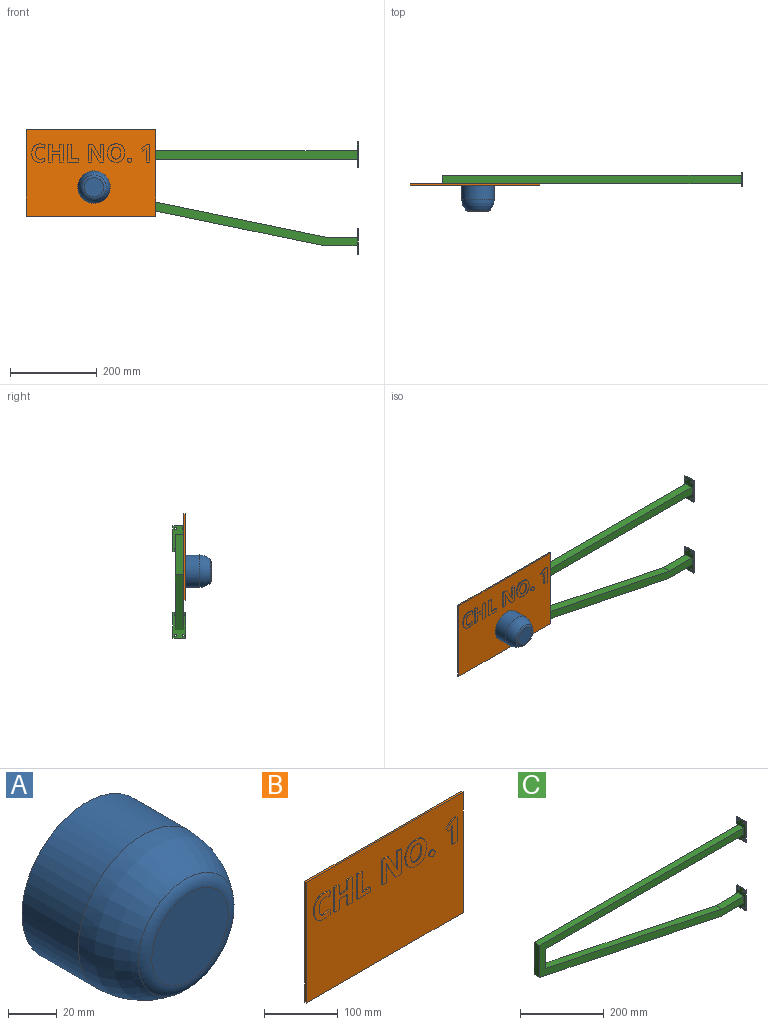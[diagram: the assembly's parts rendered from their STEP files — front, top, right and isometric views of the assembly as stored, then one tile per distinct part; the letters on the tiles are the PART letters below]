
ASSEMBLY  parts=3 mates=2
PART A: 5 faces, bbox 75x60x75 mm
  f0: cylinder r=37.5mm len=75mm, axis (0,1,0), area 7711.8mm2, adj f2,f4
  f1: plane 44.37x44.37mm, normal (0,-1,0), area 1546.4mm2, adj f3
  f2: plane 75x75mm, normal (0,1,0), area 4417.9mm2, adj f0
  f3: torus R=22.19mm, axis (0,-1,0), area 993.7mm2, adj f1,f4
  f4: torus R=0.5mm, axis (0,-1,0), area 5880.9mm2, adj f0,f3
PART B: 93 faces, bbox 300x5x200 mm
  f0: plane 300x200mm, normal (0,-1,0), area 55248.8mm2, adj f1,f2,f3,f4,f6,f7,f8,f9
  f1: plane 200x3mm, normal (1,0,0), area 600mm2, adj f0,f2,f4,f5
  f2: plane 300x3mm, normal (0,0,1), area 900mm2, adj f0,f1,f3,f5
  f3: plane 200x3mm, normal (-1,0,0), area 600mm2, adj f0,f2,f4,f5
  f4: plane 300x3mm, normal (0,0,-1), area 900mm2, adj f0,f1,f3,f5
  f5: plane 300x200mm, normal (0,1,0), area 60000mm2, adj f1,f2,f3,f4
  f6: extruded ~7.63x3.7mm, area 17.7mm2, adj f0,f7,f20,f21
  f7: extruded ~4.58x2mm, area 9.4mm2, adj f0,f6,f8,f21
  f8: extruded ~4.65x2mm, area 10.1mm2, adj f0,f7,f9,f21
  f9: plane 7.1x2.81mm, normal (0.93,0,-0.37), area 15.3mm2, adj f0,f8,f10,f21
  f10: extruded ~12.04x2.89mm, area 25mm2, adj f0,f9,f11,f21
  f11: extruded ~10.26x2.57mm, area 21.4mm2, adj f0,f10,f12,f21
  f12: extruded ~7.4x6.71mm, area 20.3mm2, adj f0,f11,f13,f21
  f13: extruded ~11.25x2.34mm, area 23.2mm2, adj f0,f12,f14,f21
  f14: extruded ~15.63x4.75mm, area 33.4mm2, adj f0,f13,f15,f21
  f15: extruded ~13.73x5.45mm, area 30.5mm2, adj f0,f14,f16,f21
  f16: extruded ~11.31x2.12mm, area 23.2mm2, adj f0,f15,f17,f21
  f17: plane 7.31x2mm, normal (1,0,0), area 14.6mm2, adj f0,f16,f18,f21
  f18: extruded ~10.49x2.16mm, area 21.5mm2, adj f0,f17,f19,f21
  f19: extruded ~13.76x10.33mm, area 39.3mm2, adj f0,f18,f20,f21
  f20: extruded ~10.31x2.7mm, area 21.7mm2, adj f0,f6,f19,f21
  f21: plane 42.29x31.34mm, normal (0,-1,0), area 594.2mm2, adj f6,f7,f8,f9,f10,f11,f12,f13
  f22: plane 8.7x2mm, normal (0,0,-1), area 17.4mm2, adj f0,f23,f33,f34
  f23: plane 41.14x2mm, normal (1,0,0), area 82.3mm2, adj f0,f22,f24,f34
  f24: plane 8.7x2mm, normal (0,0,1), area 17.4mm2, adj f0,f23,f25,f34
  f25: plane 16.13x2mm, normal (-1,0,0), area 32.3mm2, adj f0,f24,f26,f34
  f26: plane 16.29x2mm, normal (0,0,1), area 32.6mm2, adj f0,f25,f27,f34
  f27: plane 16.13x2mm, normal (1,0,0), area 32.3mm2, adj f0,f26,f28,f34
  f28: plane 8.72x2mm, normal (0,0,1), area 17.4mm2, adj f0,f27,f29,f34
  f29: plane 41.14x2mm, normal (-1,0,0), area 82.3mm2, adj f0,f28,f30,f34
  f30: plane 8.72x2mm, normal (0,0,-1), area 17.4mm2, adj f0,f29,f31,f34
  f31: plane 17.76x2mm, normal (1,0,0), area 35.5mm2, adj f0,f30,f32,f34
  f32: plane 16.29x2mm, normal (0,0,-1), area 32.6mm2, adj f0,f31,f33,f34
  f33: plane 17.76x2mm, normal (-1,0,0), area 35.5mm2, adj f0,f22,f32,f34
  f34: plane 41.14x33.71mm, normal (0,-1,0), area 834.9mm2, adj f22,f23,f24,f25,f26,f27,f28,f29
  f35: plane 41.14x2mm, normal (-1,0,0), area 82.3mm2, adj f0,f36,f40,f41
  f36: plane 25.41x2mm, normal (0,0,-1), area 50.8mm2, adj f0,f35,f37,f41
  f37: plane 7.2x2mm, normal (1,0,0), area 14.4mm2, adj f0,f36,f38,f41
  f38: plane 16.68x2mm, normal (0,0,1), area 33.4mm2, adj f0,f37,f39,f41
  f39: plane 33.94x2mm, normal (1,0,0), area 67.9mm2, adj f0,f38,f40,f41
  f40: plane 8.72x2mm, normal (0,0,1), area 17.4mm2, adj f0,f35,f39,f41
  f41: plane 41.14x25.41mm, normal (0,-1,0), area 479.1mm2, adj f35,f36,f37,f38,f39,f40
  f42: plane 11.08x2mm, normal (0,0,-1), area 22.2mm2, adj f0,f43,f55,f56
  f43: plane 41.14x2mm, normal (1,0,0), area 82.3mm2, adj f0,f42,f44,f56
  f44: plane 7.85x2mm, normal (0,0,1), area 15.7mm2, adj f0,f43,f45,f56
  f45: plane 19.48x2mm, normal (-1,0,0), area 39mm2, adj f0,f44,f46,f56
  f46: extruded ~11.34x2mm, area 22.7mm2, adj f0,f45,f47,f56
  f47: plane 2x0.2mm, normal (0,0,1), area 0.4mm2, adj f0,f46,f48,f56
  f48: plane 30.81x17.86mm, normal (0.87,0,0.5), area 71.2mm2, adj f0,f47,f49,f56
  f49: plane 11x2mm, normal (0,0,1), area 22mm2, adj f0,f48,f50,f56
  f50: plane 41.14x2mm, normal (-1,0,0), area 82.3mm2, adj f0,f49,f51,f56
  f51: plane 7.8x2mm, normal (0,0,-1), area 15.6mm2, adj f0,f50,f52,f56
  f52: plane 19.36x2mm, normal (1,0,0), area 38.7mm2, adj f0,f51,f53,f56
  f53: extruded ~11.76x2mm, area 23.5mm2, adj f0,f52,f54,f56
  f54: plane 2x0.25mm, normal (0,0,-1), area 0.5mm2, adj f0,f53,f55,f56
  f55: plane 31.12x17.9mm, normal (-0.87,0,-0.5), area 71.8mm2, adj f0,f42,f54,f56
  f56: plane 41.14x36.49mm, normal (0,-1,0), area 959mm2, adj f42,f43,f44,f45,f46,f47,f48,f49
  f57: extruded ~10.39x2.62mm, area 21.8mm2, adj f58,f70,f71,f72
  f58: extruded ~10.39x2.64mm, area 21.8mm2, adj f57,f59,f71,f72
  f59: extruded ~7.85x3.5mm, area 17.9mm2, adj f58,f60,f71,f72
  f60: extruded ~13.89x10.38mm, area 39.6mm2, adj f59,f61,f71,f72
  f61: extruded ~13.88x10.44mm, area 39.6mm2, adj f60,f70,f71,f72
  f62: extruded ~15.71x5.06mm, area 33.8mm2, adj f0,f63,f69,f71
  f63: extruded ~15.7x5.02mm, area 33.8mm2, adj f0,f62,f64,f71
  f64: extruded ~14.51x5.46mm, area 31.9mm2, adj f0,f63,f65,f71
  f65: extruded ~14.56x5.42mm, area 32mm2, adj f0,f64,f66,f71
  f66: extruded ~15.69x5.08mm, area 33.8mm2, adj f0,f65,f67,f71
  f67: extruded ~15.76x5.06mm, area 33.9mm2, adj f0,f66,f68,f71
  f68: extruded ~14.52x5.49mm, area 32mm2, adj f0,f67,f69,f71
  f69: extruded ~14.52x5.49mm, area 32mm2, adj f0,f62,f68,f71
  f70: extruded ~7.82x3.49mm, area 17.8mm2, adj f57,f61,f71,f72
  f71: plane 42.35x39.17mm, normal (0,-1,0), area 886.3mm2, adj f57,f58,f59,f60,f61,f62,f63,f64
  f72: plane 27.77x20.87mm, normal (0,-1,0), area 482.5mm2, adj f57,f58,f59,f60,f61,f70
  f73: extruded ~3.57x2mm, area 7.8mm2, adj f0,f74,f80,f81
  f74: extruded ~3.53x2mm, area 7.7mm2, adj f0,f73,f75,f81
  f75: extruded ~3.66x2mm, area 7.9mm2, adj f0,f74,f76,f81
  f76: extruded ~3.6x2mm, area 7.8mm2, adj f0,f75,f77,f81
  f77: extruded ~3.5x2mm, area 7.7mm2, adj f0,f76,f78,f81
  f78: extruded ~3.54x2mm, area 7.7mm2, adj f0,f77,f79,f81
  f79: extruded ~3.61x2mm, area 7.8mm2, adj f0,f78,f80,f81
  f80: extruded ~3.69x2mm, area 8mm2, adj f0,f73,f79,f81
  f81: plane 9.84x9.56mm, normal (0,-1,0), area 77.4mm2, adj f73,f74,f75,f76,f77,f78,f79,f80
  f82: plane 8.7x2mm, normal (0,0,-1), area 17.4mm2, adj f0,f83,f91,f92
  f83: plane 41.14x2mm, normal (1,0,0), area 82.3mm2, adj f0,f82,f84,f92
  f84: plane 7.15x2mm, normal (0,0,1), area 14.3mm2, adj f0,f83,f85,f92
  f85: plane 13.25x10.55mm, normal (-0.62,0,0.78), area 33.9mm2, adj f0,f84,f86,f92
  f86: plane 5.23x4.2mm, normal (-0.78,0,-0.63), area 13.4mm2, adj f0,f85,f87,f92
  f87: plane 4.73x3.8mm, normal (0.63,0,-0.78), area 12.1mm2, adj f0,f86,f88,f92
  f88: extruded ~3.01x2.84mm, area 8.3mm2, adj f0,f87,f89,f92
  f89: plane 4.28x2mm, normal (-1,0,0.03), area 8.6mm2, adj f0,f88,f90,f92
  f90: plane 3.91x2mm, normal (-1,0,0.02), area 7.8mm2, adj f0,f89,f91,f92
  f91: plane 23.81x2mm, normal (-1,0,0), area 47.6mm2, adj f0,f82,f90,f92
  f92: plane 41.14x20.4mm, normal (0,-1,0), area 437.7mm2, adj f82,f83,f84,f85,f86,f87,f88,f89
PART C: 30 faces, bbox 692x30x260 mm
  f0: plane 76.02x20mm, normal (0,0,-1), area 1520.4mm2, adj f3,f6,f8,f16
  f1: plane 73.98x20mm, normal (0,0,1), area 1479.6mm2, adj f2,f6,f8,f16
  f2: plane 596.02x123.15mm, normal (0.2,0,0.98), area 12172.2mm2, adj f1,f4,f6,f8
  f3: plane 613.98x126.86mm, normal (-0.2,0,-0.98), area 12538.9mm2, adj f0,f5,f6,f8
  f4: plane 56.86x20mm, normal (1,0,0), area 1137.1mm2, adj f2,f6,f7,f8
  f5: plane 93.15x20mm, normal (-1,0,0), area 1862.9mm2, adj f3,f6,f8,f9
  f6: plane 690x220mm, normal (0,-1,0), area 28955.6mm2, adj f0,f1,f2,f3,f4,f5,f7,f9
  f7: plane 670x20mm, normal (0,0,-1), area 13400mm2, adj f4,f6,f8,f15
  f8: plane 690x220mm, normal (0,1,0), area 28955.6mm2, adj f0,f1,f2,f3,f4,f5,f7,f9
  f9: plane 690x20mm, normal (0,0,1), area 13800mm2, adj f5,f6,f8,f15
  f10: plane 30x2mm, normal (0,0,-1), area 60mm2, adj f11,f13,f14,f15
  f11: plane 60x2mm, normal (0,1,0), area 120mm2, adj f10,f12,f14,f15
  f12: plane 30x2mm, normal (0,0,1), area 60mm2, adj f11,f13,f14,f15
  f13: plane 60x2mm, normal (0,-1,0), area 120mm2, adj f10,f12,f14,f15
  f14: plane 60x30mm, normal (1,0,0), area 1721.5mm2, adj f10,f11,f12,f13,f26,f27,f28,f29
  f15: plane 60x30mm, normal (-1,0,0), area 1321.5mm2, adj f6,f7,f8,f9,f10,f11,f12,f13
  f16: plane 60x30mm, normal (-1,0,0), area 1321.5mm2, adj f0,f1,f6,f8,f17,f18,f19,f20
  f17: plane 60x2mm, normal (0,1,0), area 120mm2, adj f16,f18,f20,f21
  f18: plane 30x2mm, normal (0,0,1), area 60mm2, adj f16,f17,f19,f21
  f19: plane 60x2mm, normal (0,-1,0), area 120mm2, adj f16,f18,f20,f21
  f20: plane 30x2mm, normal (0,0,-1), area 60mm2, adj f16,f17,f19,f21
  f21: plane 60x30mm, normal (1,0,0), area 1721.5mm2, adj f17,f18,f19,f20,f22,f23,f24,f25
  f22: cylinder r=2.5mm len=5mm, axis (1,0,0), area 31.4mm2, adj f16,f21
  f23: cylinder r=2.5mm len=5mm, axis (1,0,0), area 31.4mm2, adj f16,f21
  f24: cylinder r=2.5mm len=5mm, axis (1,0,0), area 31.4mm2, adj f16,f21
  f25: cylinder r=2.5mm len=5mm, axis (1,0,0), area 31.4mm2, adj f16,f21
  f26: cylinder r=2.5mm len=5mm, axis (1,0,0), area 31.4mm2, adj f14,f15
  f27: cylinder r=2.5mm len=5mm, axis (1,0,0), area 31.4mm2, adj f14,f15
  f28: cylinder r=2.5mm len=5mm, axis (1,0,0), area 31.4mm2, adj f14,f15
  f29: cylinder r=2.5mm len=5mm, axis (1,0,0), area 31.4mm2, adj f14,f15
PLACE A t=(-230.54,87.31,161.69)mm
PLACE B t=(-237.54,90.31,194.88)mm
PLACE C t=(377.18,100.31,236.33)mm
MATE planar A.f0 <-> B.f0  axis (0,1,0) through (-230.54,87.31,161.69)mm
MATE planar B.f5 <-> C.f6  axis (0,1,0) through (-237.54,90.31,194.88)mm
